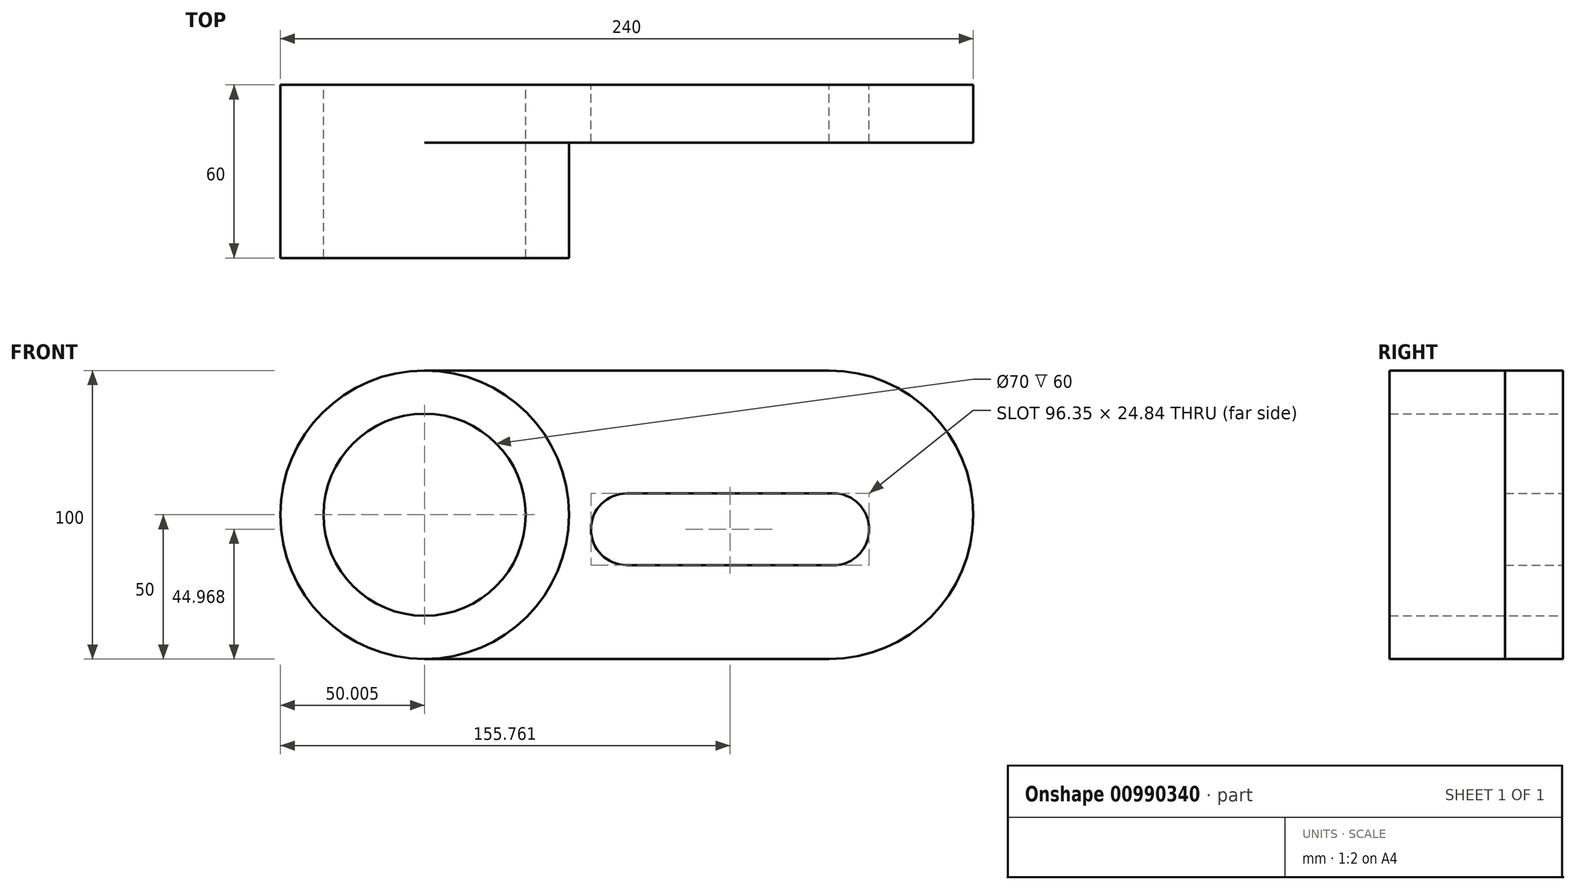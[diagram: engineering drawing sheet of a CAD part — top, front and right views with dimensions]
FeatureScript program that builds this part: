
annotation { "Feature Type Name" : "Feature", "Feature Type Description" : "" }
export const myFeature = defineFeature(function(context is Context, id is Id, definition is map)
    precondition{}
    {
        {
            var Q0;
            Q0=qCreatedBy(makeId("Front.planeOp"),FACE);
            var sketch = newSketch(context, id + "F0", { "sketchPlane" : qUnion([Q0])});
            skCircle(sketch, "E0", {"center": v(-117.76, 0) * mm, "radius": 50 * mm});
            skCircle(sketch, "E1", {"center": v(-117.76, 0) * mm, "radius": 35 * mm});
            skLineSegment(sketch, "E2", {"start": v(-117.76, 50) * mm, "end": v(22.24, 50) * mm});
            skLineSegment(sketch, "E3", {"start": v(-117.76, -50) * mm, "end": v(22.24, -50) * mm});
            skArc(sketch, "E4", {"start": v(22.24, -50) * mm, "mid": v(72.24, 0) * mm, "end": v(22.24, 50) * mm});
            skArc(sketch, "E5", {"start": v(22.24, -17.45) * mm, "mid": v(36.17, -5.03) * mm, "end": v(22.24, 7.39) * mm});
            skLineSegment(sketch, "E6", {"start": v(22.24, 7.39) * mm, "end": v(-47.76, 7.39) * mm});
            skLineSegment(sketch, "E7", {"start": v(22.24, -17.45) * mm, "end": v(-47.76, -17.45) * mm});
            skArc(sketch, "E8", {"start": v(-47.76, 7.39) * mm, "mid": v(-60.17, -5.03) * mm, "end": v(-47.76, -17.45) * mm});
            skSolve(sketch);
        }
        {
            var Q0;
            Q0=makeQuery(id+"F0.imprint","IMPRINT",FACE,{"disambiguationData":[TD([[makeQuery(id+"F0.imprint","IMPRINT",EDGE,{"derivedFrom":sQuery(id+"F0.wireOp",EDGE,"E1")}),-1.0]])]});
            extrude(context, id + "F1", {"entities" : qUnion([Q0]), "depth" : 60 * mm, "offsetDistance" : 25 * mm});
        }
        {
            var Q0;
            {var subQ1=sQuery(id+"F0.wireOp",EDGE,"E2");Q0=makeQuery(id+"F0.imprint","IMPRINT",FACE,{"disambiguationData":[TD([[makeQuery(id+"F0.imprint","IMPRINT",EDGE,{"derivedFrom":subQ1}),-1.0]])]});}
            extrude(context, id + "F2", {"entities" : qUnion([Q0]), "operationType" : NewBodyOperationType.ADD, "depth" : 20 * mm, "offsetDistance" : 25 * mm});
        }
    });
